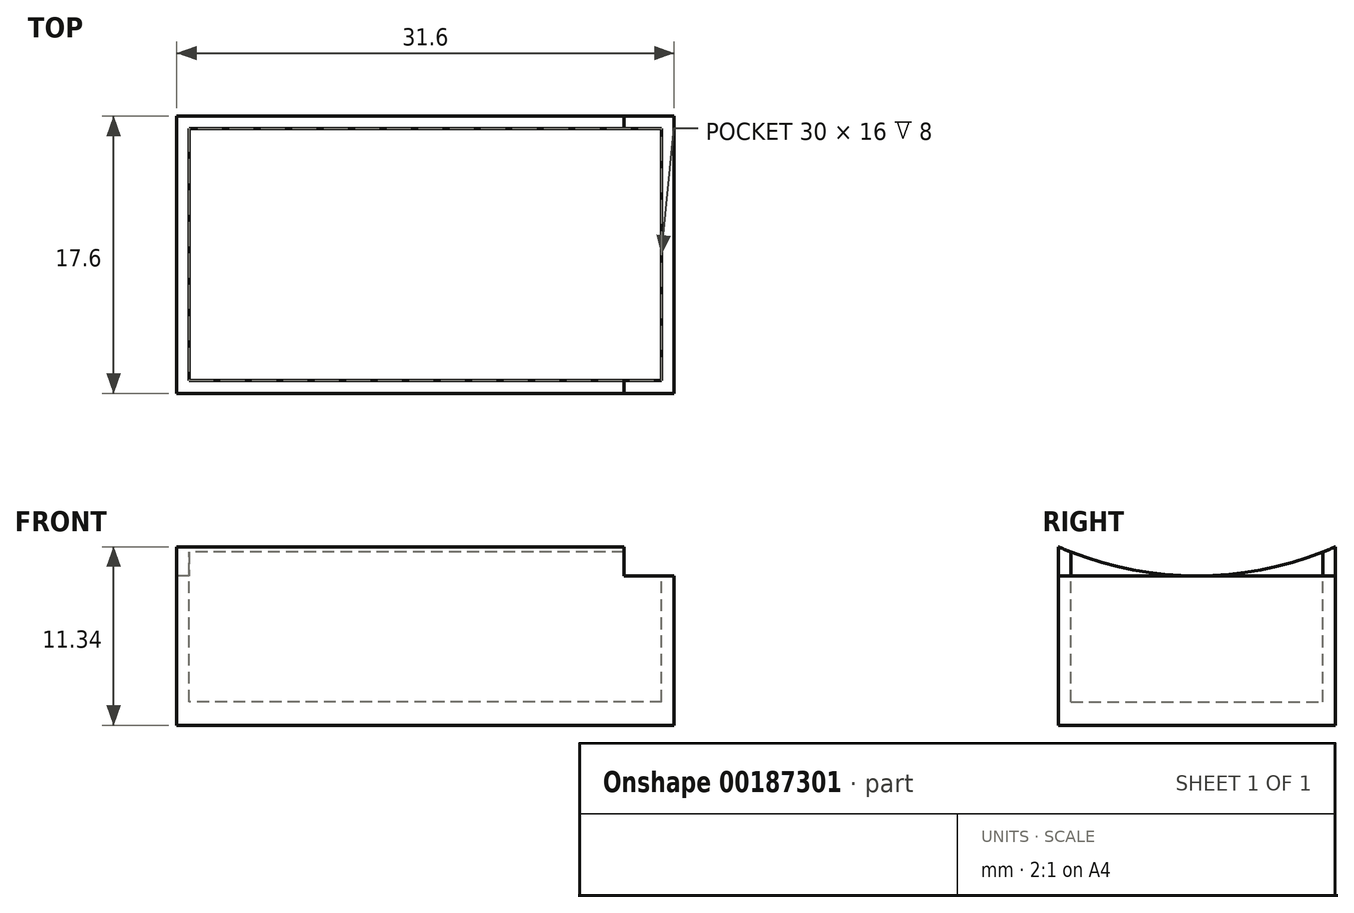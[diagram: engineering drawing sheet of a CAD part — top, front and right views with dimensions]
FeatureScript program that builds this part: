
annotation { "Feature Type Name" : "Feature", "Feature Type Description" : "" }
export const myFeature = defineFeature(function(context is Context, id is Id, definition is map)
    precondition{}
    {
        {
            var Q0;
            Q0=qCreatedBy(makeId("Top.planeOp"),FACE);
            var sketch = newSketch(context, id + "F0", { "sketchPlane" : qUnion([Q0])});
            skLineSegment(sketch, "E0.bottom", {"start": v(15.8, 8.8) * mm, "end": v(-15.8, 8.8) * mm});
            skLineSegment(sketch, "E0.top", {"start": v(15.8, -8.8) * mm, "end": v(-15.8, -8.8) * mm});
            skLineSegment(sketch, "E0.left", {"start": v(15.8, 8.8) * mm, "end": v(15.8, -8.8) * mm});
            skLineSegment(sketch, "E0.right", {"start": v(-15.8, 8.8) * mm, "end": v(-15.8, -8.8) * mm});
            skPoint(sketch, "E0.middle", {"position": v(0, 0) * mm});
            skSolve(sketch);
        }
        {
            var Q0;
            Q0 = qSketchRegion(id + "F0", true);
            extrude(context, id + "F1", {"entities" : qUnion([Q0]), "depth" : 25 * mm, "offsetDistance" : 25 * mm});
        }
        {
            var Q0;
            Q0=makeQuery(id+"F1.opExtrude","CAP_FACE",FACE,{"disambiguationData":[OSD([sQuery(id+"F0.wireOp",EDGE,"E0.bottom"),sQuery(id+"F0.wireOp",EDGE,"E0.top"),sQuery(id+"F0.wireOp",EDGE,"E0.left"),sQuery(id+"F0.wireOp",EDGE,"E0.right")])],"isStart":false});
            var sketch = newSketch(context, id + "F2", { "sketchPlane" : qUnion([Q0])});
            skLineSegment(sketch, "E1.bottom", {"start": v(15, -8) * mm, "end": v(-15, -8) * mm});
            skLineSegment(sketch, "E1.top", {"start": v(15, 8) * mm, "end": v(-15, 8) * mm});
            skLineSegment(sketch, "E1.left", {"start": v(15, -8) * mm, "end": v(15, 8) * mm});
            skLineSegment(sketch, "E1.right", {"start": v(-15, -8) * mm, "end": v(-15, 8) * mm});
            skPoint(sketch, "E1.middle", {"position": v(0, 0) * mm});
            skSolve(sketch);
        }
        {
            var Q0;
            Q0 = qSketchRegion(id + "F2", true);
            extrude(context, id + "F3", {"entities" : qUnion([Q0]), "operationType" : NewBodyOperationType.REMOVE, "oppositeDirection" : true, "depth" : 23.5 * mm, "offsetDistance" : 25 * mm});
        }
        {
            var Q0;
            Q0=qCreatedBy(makeId("Right.planeOp"),FACE);
            var sketch = newSketch(context, id + "F4", { "sketchPlane" : qUnion([Q0])});
            skCircle(sketch, "E2", {"center": v(0, 31.5) * mm, "radius": 22 * mm});
            skSolve(sketch);
        }
        {
            var Q0;
            Q0=makeQuery(id+"F4.imprint","IMPRINT",FACE,{"disambiguationData":[TD([[makeQuery(id+"F4.imprint","IMPRINT",EDGE,{"derivedFrom":sQuery(id+"F4.wireOp",EDGE,"E2")}),1.0]])]});
            extrude(context, id + "F5", {"entities" : qUnion([Q0]), "operationType" : NewBodyOperationType.REMOVE, "depth" : (15.8 - 3.2) * mm, "offsetDistance" : 25 * mm, "hasSecondDirection" : true, "secondDirectionBound" : SecondDirectionBoundingType.THROUGH_ALL, "secondDirectionOppositeDirection" : true, "secondDirectionDepth" : 25 * mm});
        }
        {
            var Q0;
            Q0=makeQuery(id+"F1.opExtrude","SWEPT_FACE",FACE,{"disambiguationData":[OSD([sQuery(id+"F0.wireOp",EDGE,"E0.left")])]});
            var sketch = newSketch(context, id + "F6", { "sketchPlane" : qUnion([Q0])});
            skLineSegment(sketch, "E3.bottom", {"start": v(12.5, 9.5) * mm, "end": v(-12.5, 9.5) * mm});
            skLineSegment(sketch, "E3.top", {"start": v(12.5, 59.5) * mm, "end": v(-12.5, 59.5) * mm});
            skLineSegment(sketch, "E3.left", {"start": v(12.5, 9.5) * mm, "end": v(12.5, 59.5) * mm});
            skLineSegment(sketch, "E3.right", {"start": v(-12.5, 9.5) * mm, "end": v(-12.5, 59.5) * mm});
            skPoint(sketch, "E3.middle", {"position": v(0, 34.5) * mm});
            skSolve(sketch);
        }
        {
            var Q0;
            Q0 = qSketchRegion(id + "F6", true);
            extrude(context, id + "F7", {"entities" : qUnion([Q0]), "operationType" : NewBodyOperationType.REMOVE, "oppositeDirection" : true, "depth" : 3.2 * mm, "offsetDistance" : 25 * mm});
        }
    });
